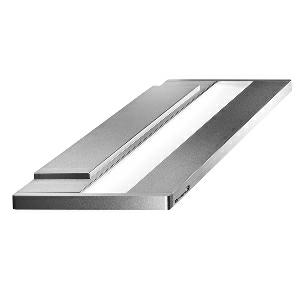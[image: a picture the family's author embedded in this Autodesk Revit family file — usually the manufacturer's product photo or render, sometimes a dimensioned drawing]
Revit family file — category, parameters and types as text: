
# Revit family: zera_bed_-_zew_11000_830_-_ul_re_nl_00813009_d84c
name_source: partatom
category: Lighting Fixtures
units: mm (PartAtom-declared; Revit-internal decimal feet)

## family parameters
Cut with Voids When Loaded = No
Host = Face
Light Source = No
Part Type = Normal
Room Calculation Point = No
Round Connector Dimension = Use Diameter
Shared = No

## types (1)
- AL+UL (1 x LED, 9800 lm, 4000K/3000K)
    Apparent Load = 109 VA
    Approval mark = CE
    CIE Flux Codes = 45 81 99 47 100
    Color Rendering = 90/80
    Color Temperature = 4000K/3000K
    Default Elevation = 2000 mm  [stored 6.56168 ft]
    Description = ZEW 11000/830|Wall-mounted luminaire|light source:   Warm white   |work equipment: Power supply unit|luminous flux: 10890 lm|light distribution: Direct/indirect|class of protection: I|technology: Switchable|mains lead: Connector 5 pin|glare control: Diffusor|special features: General light, indirect, 3000K, Ra80, DIN EN 60598-2-25, Reading light, direct, 2700K, Ra90, indir, Switch right, dir 4K 60W Ra95|
    Frequency = 50 Hz, 60 Hz
    Height = 20 mm  [stored 0.0656168 ft]
    Lamp = 1 x LED
    Lamp Light Flux = 9800 lm
    Lamp count = 1
    Length = 1050 mm
    Luminous efficacy = 90 lm/W
    Manufacturer = Waldmann
    ModVariant = No
    Model = 00813009
    Mounting Place = Wall
    Mounting Type = Surface mounted
    Number of Poles = 1
    OnlyDefault = Yes
    Power Factor = 1
    Product Name = ZERA.bed - ZEW 11000/830 - UL RE/NL
    Product group = Wall mounted Luminaire
    ProductGroupID = 20
    Protection Class = Protection class I
    Protection Degree = IP 20
    RLX_Detail_Level = 1
    RLX_Emergency_Light_Flux = 0 lm
    RLX_Emergency_Type = 0
    RLX_Emergency_Type_DB = No
    RlxData = <blob elided: 60189 chars, md5=b8d24b19>
    Socket = socket
    Standby Power = 0 W
    System Light Flux = 9800 lm
    System Power = 109 W
    Type Comments = General and Examation Light
    Type Image = zera_bed.jpg
    URL = http://relux.com
    VarID = al_ul_37f9
    Voltage = 230 V
    Voltage Range = 220-240 V
    Weight = 0.00 kg
    Width = 230 mm

note: [stored X ft] marks values corroborated as IEEE doubles in the binary element streams (Revit-internal decimal feet)

## geometry (parser evidence)
native form markers: Blend x4, Sweep x15
no freeform markers — native parametric forms only
